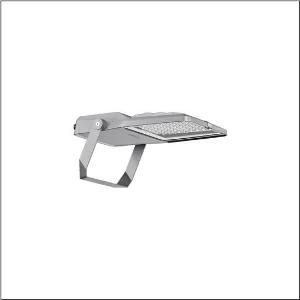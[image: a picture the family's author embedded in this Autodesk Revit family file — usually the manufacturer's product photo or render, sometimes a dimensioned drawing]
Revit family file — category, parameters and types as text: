
# Revit family: floodlight_fl_21_mini___pl64_5xa7776b2e1a_6c25
name_source: partatom
category: Lighting Fixtures
units: mm (PartAtom-declared; Revit-internal decimal feet)

## family parameters
Cut with Voids When Loaded = No
Host = Face
Light Source = No
Part Type = Normal
Room Calculation Point = No
Round Connector Dimension = Use Diameter
Shared = No

## types (1)
- --- (1 x LED, 6010 lm, 45.7 W, 3000K)
    Apparent Load = 46 VA
    CIE Flux Codes = 28 80 98 100 100
    Color Rendering = 70
    Color Temperature = 3000K
    Default Elevation = 1800 mm
    Description = Floodlight FL 21 mini, floodlight, primary light control with lens, of PMMA, primary optical cover: protective disc, of toughened safety glass, transparent, light distribution: PL64, light emission: direct distribution, installation type: surface-mounted, LED, High Power LED, rated luminous flux: 6.010lm, luminous efficacy: 132lm/W, light colour: 730, colour temperature: 3000K, control: flexible luminous flux parameterisation, time-dependent luminous flux control, constant luminous flux control, overheat protection, presetting dimming logarithmic, with terminal, 6-pole, mains connection: 220..240V, AC, 50/60Hz, start of lifetime: 46W, end of service life: 48W, reduction: 22W, luminaire housing, of diecast aluminium, powder-coated, Siteco® metallic grey (DB 702S), corrosivity category C5 mid according to DIN EN ISO 12944, sealing non-destructively replaceable, mounting bracket, of steel, galvanised, powder-coated, Siteco® metallic grey (DB 702S), Smart Interface below and above, protection rating (complete): IP66, insulation class (complete): insulation class II (safety insulation), certification: CE, ENEC, VDE, protection symbol: D, impact resistance: IK08, permissible operating ambient temperature: -40..+40°C, permissible operating ambient temperature for outdoor applications: -40..+50°C, standard: DIN EN 12944, LABS conformity tested according to VDMA 24364:2018-05, packaging unit: 1 piece

Light Distribution: PL64
    Height = 70 mm
    Lamp = 1 x LED
    Lamp Light Flux = 6010 lm
    Lamp Power = 45.7 W
    Lamp count = 1
    Length = 485 mm
    Luminous efficacy = 132 lm/W
    Manufacturer = Siteco
    ModVariant = No
    Model = 5XA7776B2E1A
    Number of Poles = 1
    OnlyDefault = Yes
    Power Factor = 1
    Product Name = Floodlight FL 21 mini | PL64
    Product group = floodlight | pylon annexe
    ProductGroupID = 6200
    Protection Class = Protection class II
    Protection Degree = IP 66
    RLX_Detail_Level = 1
    RLX_Emergency_Light_Flux = 0 lm
    RLX_Emergency_Type = 0
    RLX_Emergency_Type_DB = No
    RlxData = <blob elided: 95837 chars, md5=3b9524b9>
    Socket = socket
    Standby Power = 0 W
    System Light Flux = 6010 lm
    System Power = 46 W
    Type Comments = factory setting: luminous flux: 100 % | dim-lin: 254 | 463 mA
    Type Image = l_1006845.jpg
    URL = http://relux.com
    VarID = @adj_115661
    Voltage = 0 V
    Weight = 0.00 kg
    Width = 337 mm

## geometry (parser evidence)
native form markers: Blend x4, Sweep x12
no freeform markers — native parametric forms only
